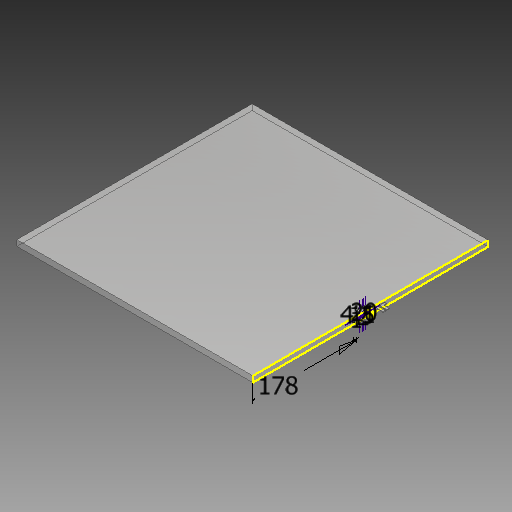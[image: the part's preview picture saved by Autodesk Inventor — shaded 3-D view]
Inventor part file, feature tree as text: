
AUTODESK INVENTOR PART (.ipt)
format: ipt  version: 2018.2 (Build 222227000, 227)  size: 148,992 bytes
history: native  units: mm
features: extrude x3, sketch x2, pattern_linear x1, projected_geometry x1
ambient origin geometry x8: Origin, YZ Plane, XZ Plane, XY Plane, X Axis, Y Axis, Z Axis, Center Point
bodies: Volumenkörper1 (feature_tree)
feature tree (7):
  extrude  "Extrusion1"  Depth=400.0mm
  sketch  "Skizze2"  dims[d2=10.0mm d3=0.0mm d4=20.0mm d5=1.0mm d6=11.0mm d7=2.0mm d8=4.5mm d10=178.0mm d11=4.0mm d12=0.0mm d15=13.0mm d16=0.0mm d17=20.0mm d19=27.0mm]
  extrude  "Extrusion2"  Depth=20.0mm
  extrude  "Extrusion4"  Depth=1.0mm
  pattern_linear  "Rechteckige Anordnung1"  Spacing1=11.0mm  [1 undecoded]
  sketch  "Skizze1"  dims[d0=400.0mm d1=400.0mm]
  projected_geometry  "Projizierte Kontur1"
note: 1 required parameter value undecoded (feature->parameter linkage not recoverable at this tier; creation-order binding heuristic only, values carry confidence <= 0.55)
